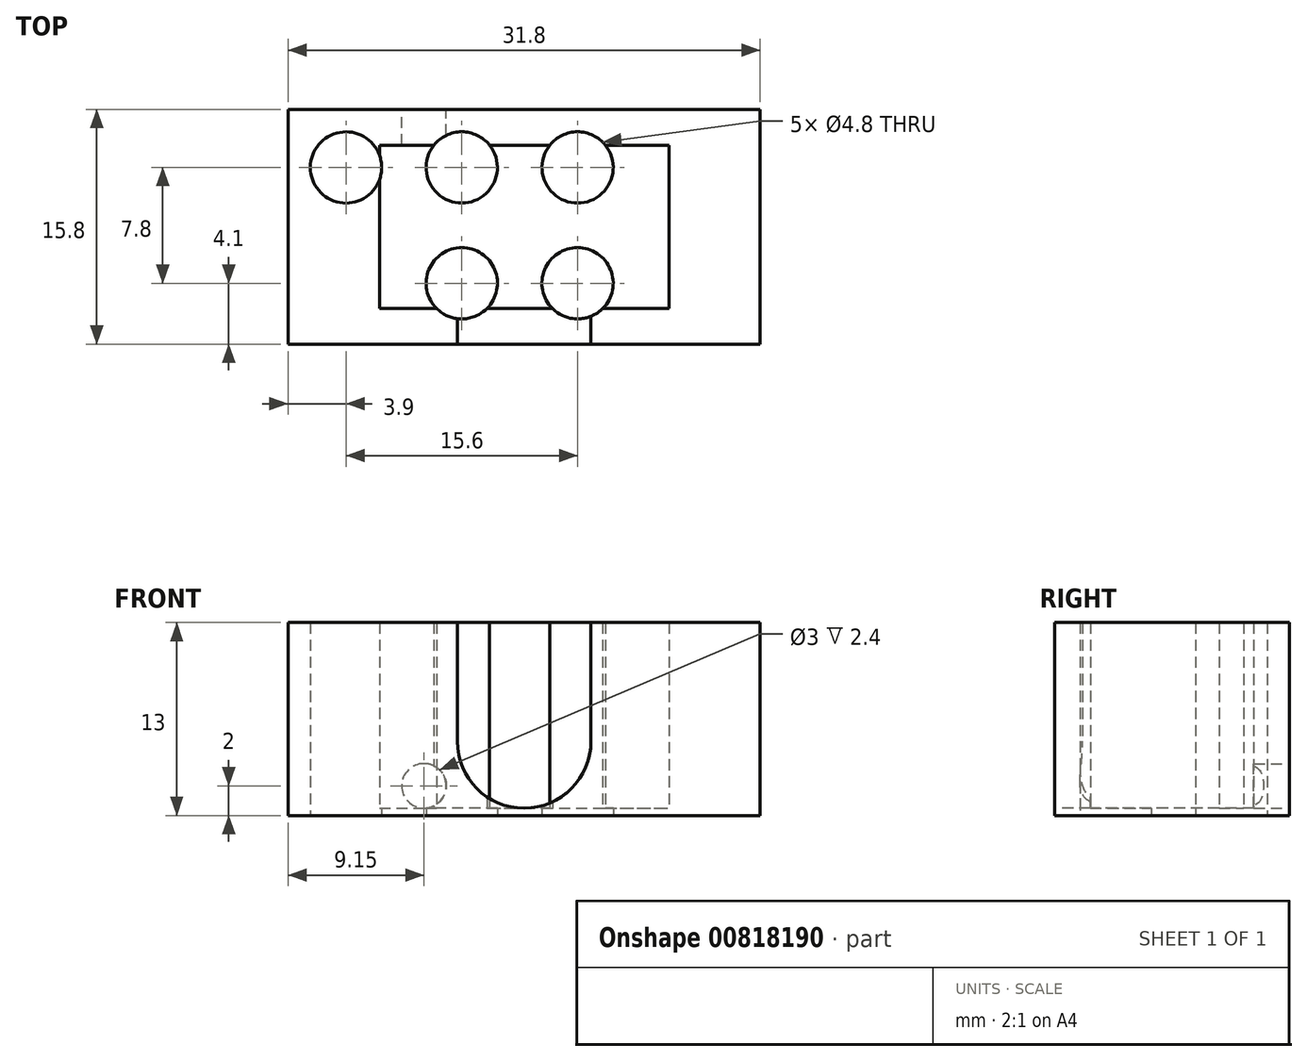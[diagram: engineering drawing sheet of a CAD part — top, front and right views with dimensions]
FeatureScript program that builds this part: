
annotation { "Feature Type Name" : "Feature", "Feature Type Description" : "" }
export const myFeature = defineFeature(function(context is Context, id is Id, definition is map)
    precondition{}
    {
        {
            var Q0;
            Q0=qCreatedBy(makeId("Top.planeOp"),FACE);
            var sketch = newSketch(context, id + "F0", { "sketchPlane" : qUnion([Q0])});
            skLineSegment(sketch, "E0.bottom", {"start": v(-15.9, 7.9) * mm, "end": v(15.9, 7.9) * mm});
            skLineSegment(sketch, "E0.top", {"start": v(-15.9, -7.9) * mm, "end": v(15.9, -7.9) * mm});
            skLineSegment(sketch, "E0.left", {"start": v(-15.9, 7.9) * mm, "end": v(-15.9, -7.9) * mm});
            skLineSegment(sketch, "E0.right", {"start": v(15.9, 7.9) * mm, "end": v(15.9, -7.9) * mm});
            skPoint(sketch, "E0.middle", {"position": v(0, 0) * mm});
            skLineSegment(sketch, "E1.bottom", {"start": v(-9.75, 5.5) * mm, "end": v(9.75, 5.5) * mm});
            skLineSegment(sketch, "E1.top", {"start": v(-9.75, -5.5) * mm, "end": v(9.75, -5.5) * mm});
            skLineSegment(sketch, "E1.left", {"start": v(-9.75, 5.5) * mm, "end": v(-9.75, -5.5) * mm});
            skLineSegment(sketch, "E1.right", {"start": v(9.75, 5.5) * mm, "end": v(9.75, -5.5) * mm});
            skCircle(sketch, "E2", {"center": v(-12, 4) * mm, "radius": 2.4 * mm});
            skCircle(sketch, "E3.0.1.0", {"center": v(-12, -3.8) * mm, "radius": 2.4 * mm});
            skCircle(sketch, "E3.1.0.0", {"center": v(-4.2, 4) * mm, "radius": 2.4 * mm});
            skCircle(sketch, "E3.1.1.0", {"center": v(-4.2, -3.8) * mm, "radius": 2.4 * mm});
            skCircle(sketch, "E3.2.0.0", {"center": v(3.6, 4) * mm, "radius": 2.4 * mm});
            skCircle(sketch, "E3.2.1.0", {"center": v(3.6, -3.8) * mm, "radius": 2.4 * mm});
            skCircle(sketch, "E3.3.0.0", {"center": v(11.4, 4) * mm, "radius": 2.4 * mm});
            skCircle(sketch, "E3.3.1.0", {"center": v(11.4, -3.8) * mm, "radius": 2.4 * mm});
            skLineSegment(sketch, "E3.direction1", {"start": v(-12, 4) * mm, "end": v(-4.2, 4) * mm, "construction": true});
            skLineSegment(sketch, "E3.direction2", {"start": v(-12, 4) * mm, "end": v(-12, -3.8) * mm, "construction": true});
            skSolve(sketch);
        }
        {
            var Q0;
            {var subQ0=sQuery(id+"F0.wireOp",EDGE,"E3.0.1.0");var subQ1=sQuery(id+"F0.wireOp",EDGE,"E1.left");var subQ2=makeQuery(id+"F0.imprint","INTERSECT",VERTEX,{"disambiguationData":[OD(0.0)],"derivedFrom":[subQ1,subQ0]});Q0=makeQuery(id+"F0.imprint","IMPRINT",FACE,{"disambiguationData":[TD([[makeQuery(id+"F0.imprint","IMPRINT",EDGE,{"disambiguationData":[TD([[subQ2,-1.0]])],"derivedFrom":subQ1}),-1.0]])]});}
            var Q1;
            {var subQ0=sQuery(id+"F0.wireOp",EDGE,"E2");var subQ1=sQuery(id+"F0.wireOp",EDGE,"E1.left");var subQ2=makeQuery(id+"F0.imprint","INTERSECT",VERTEX,{"disambiguationData":[OD(0.0)],"derivedFrom":[subQ1,subQ0]});Q1=makeQuery(id+"F0.imprint","IMPRINT",FACE,{"disambiguationData":[TD([[makeQuery(id+"F0.imprint","IMPRINT",EDGE,{"disambiguationData":[TD([[subQ2,-1.0]])],"derivedFrom":subQ1}),-1.0]])]});}
            var Q2;
            {var subQ0=sQuery(id+"F0.wireOp",EDGE,"E1.right");var subQ1=sQuery(id+"F0.wireOp",EDGE,"E1.top");var subQ2=makeQuery(id+"F0.imprint","INTERSECT",VERTEX,{"derivedFrom":[subQ1,subQ0]});Q2=makeQuery(id+"F0.imprint","IMPRINT",FACE,{"disambiguationData":[TD([[makeQuery(id+"F0.imprint","IMPRINT",EDGE,{"disambiguationData":[TD([[subQ2,1.0]])],"derivedFrom":subQ1}),-1.0]])]});}
            var Q3;
            {var subQ0=sQuery(id+"F0.wireOp",EDGE,"E1.right");var subQ1=sQuery(id+"F0.wireOp",EDGE,"E1.bottom");var subQ2=makeQuery(id+"F0.imprint","INTERSECT",VERTEX,{"derivedFrom":[subQ1,subQ0]});Q3=makeQuery(id+"F0.imprint","IMPRINT",FACE,{"disambiguationData":[TD([[makeQuery(id+"F0.imprint","IMPRINT",EDGE,{"disambiguationData":[TD([[subQ2,1.0]])],"derivedFrom":subQ1}),1.0]])]});}
            var Q4;
            {var subQ0=sQuery(id+"F0.wireOp",EDGE,"E3.1.0.0");var subQ1=sQuery(id+"F0.wireOp",EDGE,"E1.bottom");var subQ2=makeQuery(id+"F0.imprint","INTERSECT",VERTEX,{"disambiguationData":[OD(0.0)],"derivedFrom":[subQ1,subQ0]});Q4=makeQuery(id+"F0.imprint","IMPRINT",FACE,{"disambiguationData":[TD([[makeQuery(id+"F0.imprint","IMPRINT",EDGE,{"disambiguationData":[TD([[subQ2,-1.0]])],"derivedFrom":subQ1}),1.0]])]});}
            var Q5;
            {var subQ0=sQuery(id+"F0.wireOp",EDGE,"E3.2.1.0");var subQ1=sQuery(id+"F0.wireOp",EDGE,"E1.top");var subQ2=makeQuery(id+"F0.imprint","INTERSECT",VERTEX,{"disambiguationData":[OD(0.0)],"derivedFrom":[subQ1,subQ0]});Q5=makeQuery(id+"F0.imprint","IMPRINT",FACE,{"disambiguationData":[TD([[makeQuery(id+"F0.imprint","IMPRINT",EDGE,{"disambiguationData":[TD([[subQ2,-1.0]])],"derivedFrom":subQ1}),-1.0]])]});}
            var Q6;
            Q6=makeQuery(id+"F0.imprint","IMPRINT",FACE,{"disambiguationData":[TD([[makeQuery(id+"F0.imprint","IMPRINT",EDGE,{"derivedFrom":sQuery(id+"F0.wireOp",EDGE,"E0.bottom")}),-1.0]])]});
            var Q7;
            {var subQ0=sQuery(id+"F0.wireOp",EDGE,"E3.1.1.0");var subQ1=sQuery(id+"F0.wireOp",EDGE,"E1.top");var subQ2=makeQuery(id+"F0.imprint","INTERSECT",VERTEX,{"disambiguationData":[OD(0.0)],"derivedFrom":[subQ1,subQ0]});Q7=makeQuery(id+"F0.imprint","IMPRINT",FACE,{"disambiguationData":[TD([[makeQuery(id+"F0.imprint","IMPRINT",EDGE,{"disambiguationData":[TD([[subQ2,-1.0]])],"derivedFrom":subQ1}),-1.0]])]});}
            var Q8;
            {var subQ0=sQuery(id+"F0.wireOp",EDGE,"E3.2.0.0");var subQ1=sQuery(id+"F0.wireOp",EDGE,"E1.bottom");var subQ2=makeQuery(id+"F0.imprint","INTERSECT",VERTEX,{"disambiguationData":[OD(0.0)],"derivedFrom":[subQ1,subQ0]});Q8=makeQuery(id+"F0.imprint","IMPRINT",FACE,{"disambiguationData":[TD([[makeQuery(id+"F0.imprint","IMPRINT",EDGE,{"disambiguationData":[TD([[subQ2,-1.0]])],"derivedFrom":subQ1}),1.0]])]});}
            extrude(context, id + "F1", {"entities" : qUnion([Q0, Q1, Q2, Q3, Q4, Q5, Q6, Q7, Q8]), "depth" : 15 * mm, "offsetDistance" : 25 * mm});
        }
        {
            var Q0;
            Q0=makeQuery(id+"F1.opExtrude","SWEPT_FACE",FACE,{"disambiguationData":[OSD([sQuery(id+"F0.wireOp",EDGE,"E0.top")])]});
            var sketch = newSketch(context, id + "F2", { "sketchPlane" : qUnion([Q0])});
            skLineSegment(sketch, "E4", {"start": v(-4.5, 15) * mm, "end": v(-4.5, 7) * mm});
            skLineSegment(sketch, "E5", {"start": v(4.5, 15) * mm, "end": v(4.5, 7) * mm});
            skArc(sketch, "E6", {"start": v(-4.5, 7) * mm, "mid": v(0, 2.5) * mm, "end": v(4.5, 7) * mm});
            skSolve(sketch);
        }
        {
            var Q0;
            {var subQ0=sQuery(id+"F2.wireOp",EDGE,"E4");Q0=makeQuery(id+"F2.imprint","IMPRINT",FACE,{"disambiguationData":[TD([[makeQuery(id+"F2.imprint","IMPRINT",EDGE,{"derivedFrom":subQ0}),1.0]])]});}
            extrude(context, id + "F3", {"entities" : qUnion([Q0]), "operationType" : NewBodyOperationType.REMOVE, "endBound" : BoundingType.UP_TO_NEXT, "oppositeDirection" : true, "depth" : 25 * mm, "offsetDistance" : 25 * mm});
        }
        {
            var Q0;
            {var subQ5=sQuery(id+"F0.wireOp",EDGE,"E1.left");var subQ13=sQuery(id+"F0.wireOp",EDGE,"E1.bottom");var subQ14=makeQuery(id+"F0.imprint","INTERSECT",VERTEX,{"derivedFrom":[subQ13,subQ5]});Q0=makeQuery(id+"F0.imprint","IMPRINT",FACE,{"disambiguationData":[TD([[makeQuery(id+"F0.imprint","IMPRINT",EDGE,{"disambiguationData":[TD([[subQ14,-1.0]])],"derivedFrom":subQ13}),-1.0]])]});}
            var Q1;
            {var subQ0=sQuery(id+"F0.wireOp",EDGE,"E3.2.1.0");var subQ1=sQuery(id+"F0.wireOp",EDGE,"E1.top");var subQ2=makeQuery(id+"F0.imprint","INTERSECT",VERTEX,{"disambiguationData":[OD(0.0)],"derivedFrom":[subQ1,subQ0]});Q1=makeQuery(id+"F0.imprint","IMPRINT",FACE,{"disambiguationData":[TD([[makeQuery(id+"F0.imprint","IMPRINT",EDGE,{"disambiguationData":[TD([[subQ2,-1.0]])],"derivedFrom":subQ1}),1.0]])]});}
            var Q2;
            {var subQ0=sQuery(id+"F0.wireOp",EDGE,"E3.1.1.0");var subQ1=sQuery(id+"F0.wireOp",EDGE,"E1.top");var subQ2=makeQuery(id+"F0.imprint","INTERSECT",VERTEX,{"disambiguationData":[OD(0.0)],"derivedFrom":[subQ1,subQ0]});Q2=makeQuery(id+"F0.imprint","IMPRINT",FACE,{"disambiguationData":[TD([[makeQuery(id+"F0.imprint","IMPRINT",EDGE,{"disambiguationData":[TD([[subQ2,-1.0]])],"derivedFrom":subQ1}),1.0]])]});}
            var Q3;
            {var subQ0=sQuery(id+"F0.wireOp",EDGE,"E3.1.0.0");var subQ1=sQuery(id+"F0.wireOp",EDGE,"E1.bottom");var subQ2=makeQuery(id+"F0.imprint","INTERSECT",VERTEX,{"disambiguationData":[OD(0.0)],"derivedFrom":[subQ1,subQ0]});Q3=makeQuery(id+"F0.imprint","IMPRINT",FACE,{"disambiguationData":[TD([[makeQuery(id+"F0.imprint","IMPRINT",EDGE,{"disambiguationData":[TD([[subQ2,-1.0]])],"derivedFrom":subQ1}),-1.0]])]});}
            var Q4;
            {var subQ0=sQuery(id+"F0.wireOp",EDGE,"E3.2.0.0");var subQ1=sQuery(id+"F0.wireOp",EDGE,"E1.bottom");var subQ2=makeQuery(id+"F0.imprint","INTERSECT",VERTEX,{"disambiguationData":[OD(0.0)],"derivedFrom":[subQ1,subQ0]});Q4=makeQuery(id+"F0.imprint","IMPRINT",FACE,{"disambiguationData":[TD([[makeQuery(id+"F0.imprint","IMPRINT",EDGE,{"disambiguationData":[TD([[subQ2,-1.0]])],"derivedFrom":subQ1}),-1.0]])]});}
            var Q5;
            {var subQ0=sQuery(id+"F0.wireOp",EDGE,"E1.right");var subQ1=sQuery(id+"F0.wireOp",EDGE,"E1.top");var subQ2=makeQuery(id+"F0.imprint","INTERSECT",VERTEX,{"derivedFrom":[subQ1,subQ0]});Q5=makeQuery(id+"F0.imprint","IMPRINT",FACE,{"disambiguationData":[TD([[makeQuery(id+"F0.imprint","IMPRINT",EDGE,{"disambiguationData":[TD([[subQ2,1.0]])],"derivedFrom":subQ1}),1.0]])]});}
            var Q6;
            {var subQ0=sQuery(id+"F0.wireOp",EDGE,"E1.right");var subQ1=sQuery(id+"F0.wireOp",EDGE,"E1.bottom");var subQ2=makeQuery(id+"F0.imprint","INTERSECT",VERTEX,{"derivedFrom":[subQ1,subQ0]});Q6=makeQuery(id+"F0.imprint","IMPRINT",FACE,{"disambiguationData":[TD([[makeQuery(id+"F0.imprint","IMPRINT",EDGE,{"disambiguationData":[TD([[subQ2,1.0]])],"derivedFrom":subQ1}),-1.0]])]});}
            var Q7;
            {var subQ0=sQuery(id+"F0.wireOp",EDGE,"E2");var subQ1=sQuery(id+"F0.wireOp",EDGE,"E1.left");var subQ2=makeQuery(id+"F0.imprint","INTERSECT",VERTEX,{"disambiguationData":[OD(0.0)],"derivedFrom":[subQ1,subQ0]});Q7=makeQuery(id+"F0.imprint","IMPRINT",FACE,{"disambiguationData":[TD([[makeQuery(id+"F0.imprint","IMPRINT",EDGE,{"disambiguationData":[TD([[subQ2,-1.0]])],"derivedFrom":subQ1}),1.0]])]});}
            var Q8;
            {var subQ0=sQuery(id+"F0.wireOp",EDGE,"E3.0.1.0");var subQ1=sQuery(id+"F0.wireOp",EDGE,"E1.left");var subQ2=makeQuery(id+"F0.imprint","INTERSECT",VERTEX,{"disambiguationData":[OD(0.0)],"derivedFrom":[subQ1,subQ0]});Q8=makeQuery(id+"F0.imprint","IMPRINT",FACE,{"disambiguationData":[TD([[makeQuery(id+"F0.imprint","IMPRINT",EDGE,{"disambiguationData":[TD([[subQ2,-1.0]])],"derivedFrom":subQ1}),1.0]])]});}
            extrude(context, id + "F4", {"entities" : qUnion([Q0, Q1, Q2, Q3, Q4, Q5, Q6, Q7, Q8]), "operationType" : NewBodyOperationType.ADD, "depth" : 2.5 * mm, "offsetDistance" : 25 * mm});
        }
        {
            var Q0;
            Q0=makeQuery(id+"F1.opExtrude","SWEPT_FACE",FACE,{"disambiguationData":[OSD([sQuery(id+"F0.wireOp",EDGE,"E0.bottom")])]});
            var sketch = newSketch(context, id + "F5", { "sketchPlane" : qUnion([Q0])});
            skCircle(sketch, "E7", {"center": v(6.75, 4) * mm, "radius": 1.5 * mm});
            skSolve(sketch);
        }
        {
            var Q0;
            Q0=makeQuery(id+"F5.imprint","IMPRINT",FACE,{"disambiguationData":[TD([[makeQuery(id+"F5.imprint","IMPRINT",EDGE,{"derivedFrom":sQuery(id+"F5.wireOp",EDGE,"E7")}),1.0]])]});
            extrude(context, id + "F6", {"entities" : qUnion([Q0]), "operationType" : NewBodyOperationType.REMOVE, "endBound" : BoundingType.UP_TO_NEXT, "oppositeDirection" : true, "depth" : 25 * mm, "offsetDistance" : 25 * mm});
        }
        {
            var Q0;
            {var subQ0=sQuery(id+"F0.wireOp",EDGE,"E1.right");var subQ1=sQuery(id+"F0.wireOp",EDGE,"E1.bottom");var subQ2=makeQuery(id+"F0.imprint","INTERSECT",VERTEX,{"derivedFrom":[subQ1,subQ0]});Q0=makeQuery(id+"F0.imprint","IMPRINT",FACE,{"disambiguationData":[TD([[makeQuery(id+"F0.imprint","IMPRINT",EDGE,{"disambiguationData":[TD([[subQ2,1.0]])],"derivedFrom":subQ1}),1.0]])]});}
            var Q1;
            {var subQ0=sQuery(id+"F0.wireOp",EDGE,"E1.right");var subQ1=sQuery(id+"F0.wireOp",EDGE,"E1.bottom");var subQ2=makeQuery(id+"F0.imprint","INTERSECT",VERTEX,{"derivedFrom":[subQ1,subQ0]});Q1=makeQuery(id+"F0.imprint","IMPRINT",FACE,{"disambiguationData":[TD([[makeQuery(id+"F0.imprint","IMPRINT",EDGE,{"disambiguationData":[TD([[subQ2,1.0]])],"derivedFrom":subQ1}),-1.0]])]});}
            var Q2;
            {var subQ0=sQuery(id+"F0.wireOp",EDGE,"E3.2.0.0");var subQ1=sQuery(id+"F0.wireOp",EDGE,"E1.bottom");var subQ2=makeQuery(id+"F0.imprint","INTERSECT",VERTEX,{"disambiguationData":[OD(0.0)],"derivedFrom":[subQ1,subQ0]});Q2=makeQuery(id+"F0.imprint","IMPRINT",FACE,{"disambiguationData":[TD([[makeQuery(id+"F0.imprint","IMPRINT",EDGE,{"disambiguationData":[TD([[subQ2,-1.0]])],"derivedFrom":subQ1}),-1.0]])]});}
            var Q3;
            {var subQ0=sQuery(id+"F0.wireOp",EDGE,"E3.2.0.0");var subQ1=sQuery(id+"F0.wireOp",EDGE,"E1.bottom");var subQ2=makeQuery(id+"F0.imprint","INTERSECT",VERTEX,{"disambiguationData":[OD(0.0)],"derivedFrom":[subQ1,subQ0]});Q3=makeQuery(id+"F0.imprint","IMPRINT",FACE,{"disambiguationData":[TD([[makeQuery(id+"F0.imprint","IMPRINT",EDGE,{"disambiguationData":[TD([[subQ2,-1.0]])],"derivedFrom":subQ1}),1.0]])]});}
            var Q4;
            {var subQ0=sQuery(id+"F0.wireOp",EDGE,"E3.1.0.0");var subQ1=sQuery(id+"F0.wireOp",EDGE,"E1.bottom");var subQ2=makeQuery(id+"F0.imprint","INTERSECT",VERTEX,{"disambiguationData":[OD(0.0)],"derivedFrom":[subQ1,subQ0]});Q4=makeQuery(id+"F0.imprint","IMPRINT",FACE,{"disambiguationData":[TD([[makeQuery(id+"F0.imprint","IMPRINT",EDGE,{"disambiguationData":[TD([[subQ2,-1.0]])],"derivedFrom":subQ1}),-1.0]])]});}
            var Q5;
            {var subQ0=sQuery(id+"F0.wireOp",EDGE,"E3.1.0.0");var subQ1=sQuery(id+"F0.wireOp",EDGE,"E1.bottom");var subQ2=makeQuery(id+"F0.imprint","INTERSECT",VERTEX,{"disambiguationData":[OD(0.0)],"derivedFrom":[subQ1,subQ0]});Q5=makeQuery(id+"F0.imprint","IMPRINT",FACE,{"disambiguationData":[TD([[makeQuery(id+"F0.imprint","IMPRINT",EDGE,{"disambiguationData":[TD([[subQ2,-1.0]])],"derivedFrom":subQ1}),1.0]])]});}
            var Q6;
            {var subQ0=sQuery(id+"F0.wireOp",EDGE,"E2");var subQ1=sQuery(id+"F0.wireOp",EDGE,"E1.left");var subQ2=makeQuery(id+"F0.imprint","INTERSECT",VERTEX,{"disambiguationData":[OD(0.0)],"derivedFrom":[subQ1,subQ0]});Q6=makeQuery(id+"F0.imprint","IMPRINT",FACE,{"disambiguationData":[TD([[makeQuery(id+"F0.imprint","IMPRINT",EDGE,{"disambiguationData":[TD([[subQ2,-1.0]])],"derivedFrom":subQ1}),-1.0]])]});}
            var Q7;
            {var subQ0=sQuery(id+"F0.wireOp",EDGE,"E2");var subQ1=sQuery(id+"F0.wireOp",EDGE,"E1.left");var subQ2=makeQuery(id+"F0.imprint","INTERSECT",VERTEX,{"disambiguationData":[OD(0.0)],"derivedFrom":[subQ1,subQ0]});Q7=makeQuery(id+"F0.imprint","IMPRINT",FACE,{"disambiguationData":[TD([[makeQuery(id+"F0.imprint","IMPRINT",EDGE,{"disambiguationData":[TD([[subQ2,-1.0]])],"derivedFrom":subQ1}),1.0]])]});}
            var Q8;
            {var subQ0=sQuery(id+"F0.wireOp",EDGE,"E3.0.1.0");var subQ1=sQuery(id+"F0.wireOp",EDGE,"E1.left");var subQ2=makeQuery(id+"F0.imprint","INTERSECT",VERTEX,{"disambiguationData":[OD(0.0)],"derivedFrom":[subQ1,subQ0]});Q8=makeQuery(id+"F0.imprint","IMPRINT",FACE,{"disambiguationData":[TD([[makeQuery(id+"F0.imprint","IMPRINT",EDGE,{"disambiguationData":[TD([[subQ2,-1.0]])],"derivedFrom":subQ1}),-1.0]])]});}
            var Q9;
            {var subQ0=sQuery(id+"F0.wireOp",EDGE,"E3.0.1.0");var subQ1=sQuery(id+"F0.wireOp",EDGE,"E1.left");var subQ2=makeQuery(id+"F0.imprint","INTERSECT",VERTEX,{"disambiguationData":[OD(0.0)],"derivedFrom":[subQ1,subQ0]});Q9=makeQuery(id+"F0.imprint","IMPRINT",FACE,{"disambiguationData":[TD([[makeQuery(id+"F0.imprint","IMPRINT",EDGE,{"disambiguationData":[TD([[subQ2,-1.0]])],"derivedFrom":subQ1}),1.0]])]});}
            var Q10;
            {var subQ0=sQuery(id+"F0.wireOp",EDGE,"E3.1.1.0");var subQ1=sQuery(id+"F0.wireOp",EDGE,"E1.top");var subQ2=makeQuery(id+"F0.imprint","INTERSECT",VERTEX,{"disambiguationData":[OD(0.0)],"derivedFrom":[subQ1,subQ0]});Q10=makeQuery(id+"F0.imprint","IMPRINT",FACE,{"disambiguationData":[TD([[makeQuery(id+"F0.imprint","IMPRINT",EDGE,{"disambiguationData":[TD([[subQ2,-1.0]])],"derivedFrom":subQ1}),1.0]])]});}
            var Q11;
            {var subQ0=sQuery(id+"F0.wireOp",EDGE,"E3.1.1.0");var subQ1=sQuery(id+"F0.wireOp",EDGE,"E1.top");var subQ2=makeQuery(id+"F0.imprint","INTERSECT",VERTEX,{"disambiguationData":[OD(0.0)],"derivedFrom":[subQ1,subQ0]});Q11=makeQuery(id+"F0.imprint","IMPRINT",FACE,{"disambiguationData":[TD([[makeQuery(id+"F0.imprint","IMPRINT",EDGE,{"disambiguationData":[TD([[subQ2,-1.0]])],"derivedFrom":subQ1}),-1.0]])]});}
            var Q12;
            {var subQ0=sQuery(id+"F0.wireOp",EDGE,"E3.2.1.0");var subQ1=sQuery(id+"F0.wireOp",EDGE,"E1.top");var subQ2=makeQuery(id+"F0.imprint","INTERSECT",VERTEX,{"disambiguationData":[OD(0.0)],"derivedFrom":[subQ1,subQ0]});Q12=makeQuery(id+"F0.imprint","IMPRINT",FACE,{"disambiguationData":[TD([[makeQuery(id+"F0.imprint","IMPRINT",EDGE,{"disambiguationData":[TD([[subQ2,-1.0]])],"derivedFrom":subQ1}),1.0]])]});}
            var Q13;
            {var subQ0=sQuery(id+"F0.wireOp",EDGE,"E3.2.1.0");var subQ1=sQuery(id+"F0.wireOp",EDGE,"E1.top");var subQ2=makeQuery(id+"F0.imprint","INTERSECT",VERTEX,{"disambiguationData":[OD(0.0)],"derivedFrom":[subQ1,subQ0]});Q13=makeQuery(id+"F0.imprint","IMPRINT",FACE,{"disambiguationData":[TD([[makeQuery(id+"F0.imprint","IMPRINT",EDGE,{"disambiguationData":[TD([[subQ2,-1.0]])],"derivedFrom":subQ1}),-1.0]])]});}
            var Q14;
            {var subQ0=sQuery(id+"F0.wireOp",EDGE,"E1.right");var subQ1=sQuery(id+"F0.wireOp",EDGE,"E1.top");var subQ2=makeQuery(id+"F0.imprint","INTERSECT",VERTEX,{"derivedFrom":[subQ1,subQ0]});Q14=makeQuery(id+"F0.imprint","IMPRINT",FACE,{"disambiguationData":[TD([[makeQuery(id+"F0.imprint","IMPRINT",EDGE,{"disambiguationData":[TD([[subQ2,1.0]])],"derivedFrom":subQ1}),-1.0]])]});}
            var Q15;
            {var subQ0=sQuery(id+"F0.wireOp",EDGE,"E1.right");var subQ1=sQuery(id+"F0.wireOp",EDGE,"E1.top");var subQ2=makeQuery(id+"F0.imprint","INTERSECT",VERTEX,{"derivedFrom":[subQ1,subQ0]});Q15=makeQuery(id+"F0.imprint","IMPRINT",FACE,{"disambiguationData":[TD([[makeQuery(id+"F0.imprint","IMPRINT",EDGE,{"disambiguationData":[TD([[subQ2,1.0]])],"derivedFrom":subQ1}),1.0]])]});}
            extrude(context, id + "F7", {"entities" : qUnion([Q0, Q1, Q2, Q3, Q4, Q5, Q6, Q7, Q8, Q9, Q10, Q11, Q12, Q13, Q14, Q15]), "operationType" : NewBodyOperationType.REMOVE, "depth" : 2 * mm, "offsetDistance" : 25 * mm});
        }
    });
